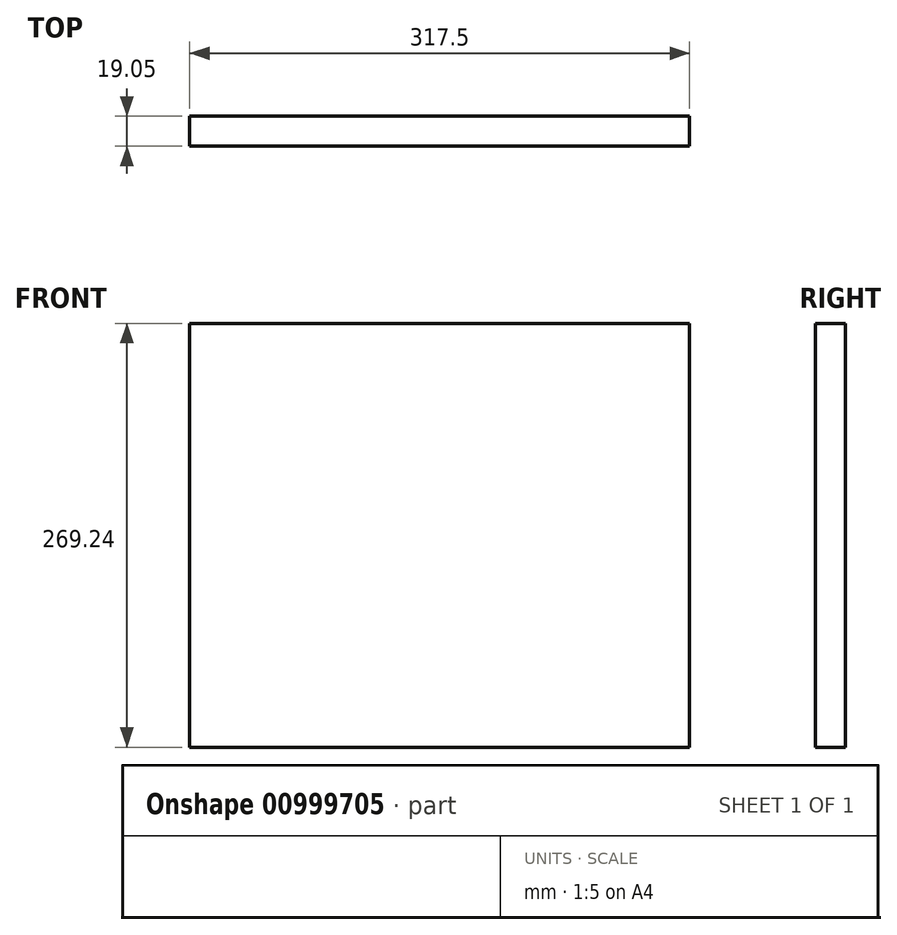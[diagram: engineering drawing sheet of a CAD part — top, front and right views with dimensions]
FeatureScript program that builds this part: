
annotation { "Feature Type Name" : "Feature", "Feature Type Description" : "" }
export const myFeature = defineFeature(function(context is Context, id is Id, definition is map)
    precondition{}
    {
        {
            var Q0;
            Q0=qCreatedBy(makeId("Front.planeOp"),FACE);
            var sketch = newSketch(context, id + "F0", { "sketchPlane" : qUnion([Q0])});
            skLineSegment(sketch, "E0.bottom", {"start": v(-158.75, -134.62) * mm, "end": v(158.75, -134.62) * mm});
            skLineSegment(sketch, "E0.top", {"start": v(-158.75, 134.62) * mm, "end": v(158.75, 134.62) * mm});
            skLineSegment(sketch, "E0.left", {"start": v(-158.75, -134.62) * mm, "end": v(-158.75, 134.62) * mm});
            skLineSegment(sketch, "E0.right", {"start": v(158.75, -134.62) * mm, "end": v(158.75, 134.62) * mm});
            skPoint(sketch, "E0.middle", {"position": v(0, 0) * mm});
            skSolve(sketch);
        }
        {
            var Q0;
            Q0=makeQuery(id+"F0.imprint","IMPRINT",FACE,{"disambiguationData":[TD([[makeQuery(id+"F0.imprint","IMPRINT",EDGE,{"derivedFrom":sQuery(id+"F0.wireOp",EDGE,"E0.bottom")}),1.0]])]});
            extrude(context, id + "F1", {"entities" : qUnion([Q0]), "depth" : 19.05 * mm, "offsetDistance" : 25.4 * mm});
        }
    });
